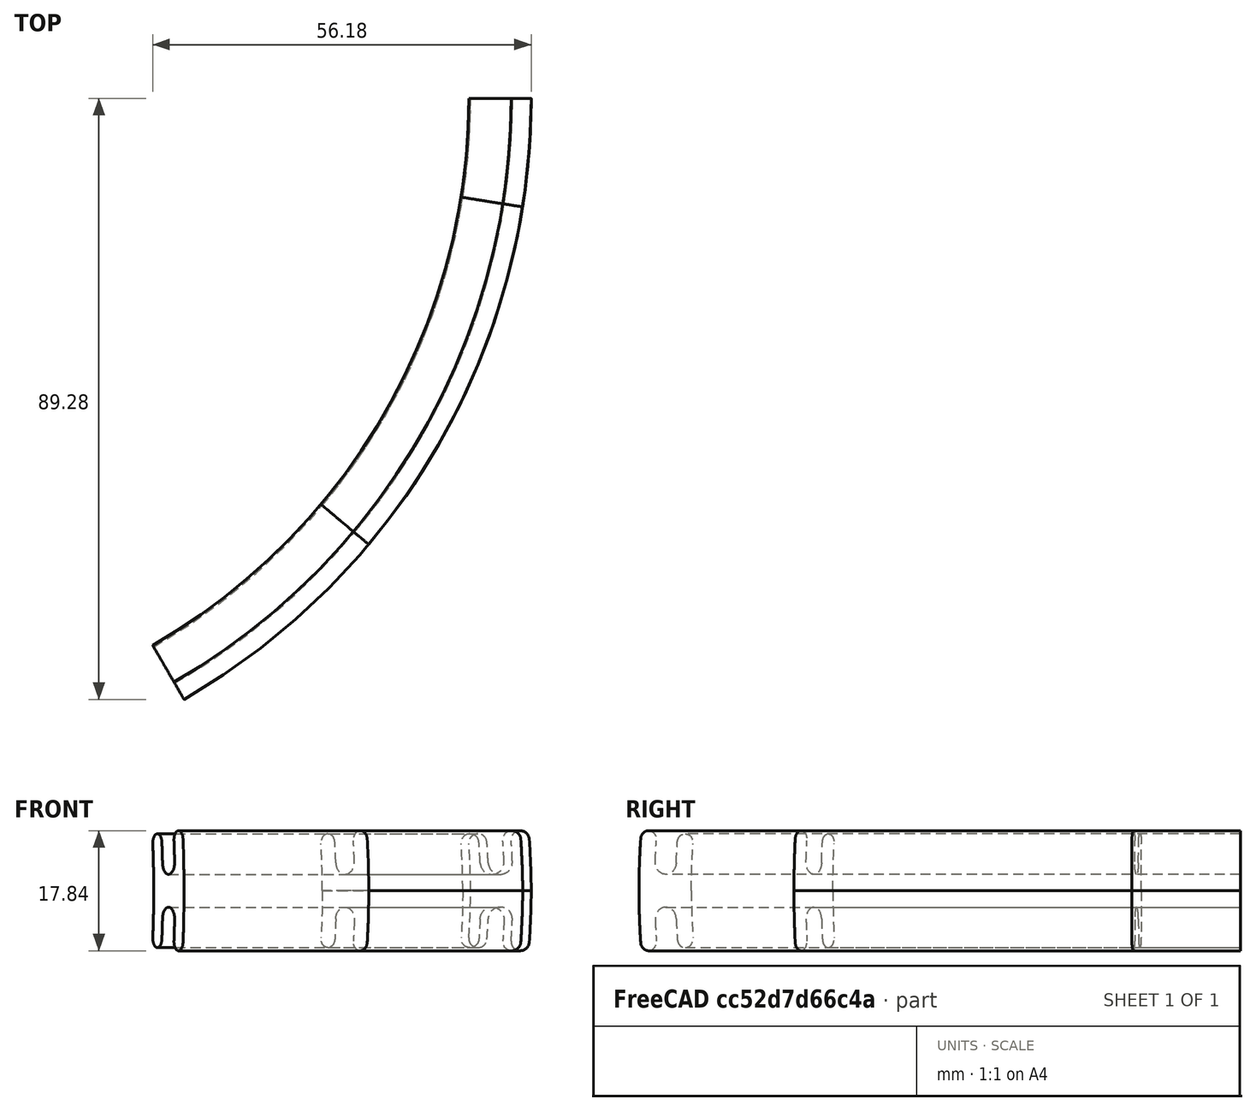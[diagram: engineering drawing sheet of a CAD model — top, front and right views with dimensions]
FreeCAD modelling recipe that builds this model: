
FCSTD DOCUMENT  (FreeCAD 0.16R6707 (Git))
Label: sphere clip
License: All rights reserved
LicenseURL: http://en.wikipedia.org/wiki/All_rights_reserved
objects: Part::Feature×3, Sketcher::SketchObject×2, PartDesign::Revolution×1
note: 7 computed .brp shape members not serialized (recipe doc carries the construction recipe); baked Part::Feature solids carry a one-line shape summary decoded from their .brp

FEATURE [Sketcher::SketchObject] Sketch  label="guide"
  Placement = pos=(0,0,0) rot=(-1,0,0;4.71239rad)
  sketch-geometry (4):
    g0: LineSegment [constr] StartX=0 StartY=4.23777 StartZ=0 EndX=100 EndY=4.23777 EndZ=0
    g1: LineSegment [constr] StartX=0 StartY=96.2378 StartZ=0 EndX=27.5 EndY=96.2378 EndZ=0
    g2: ArcOfCircle [constr] CenterX=0 CenterY=0 CenterZ=0 NormalX=0 NormalY=0 NormalZ=1 Radius=100.09 StartAngle=0 EndAngle=1.5708
    g3: ArcOfCircle [constr] CenterX=0 CenterY=0 CenterZ=0 NormalX=0 NormalY=0 NormalZ=1 Radius=97.0898 StartAngle=0 EndAngle=1.5708
  constraints (17):
    c: PointOnObject(g0,g-2)
    c: Horizontal(g0)
    c: DistanceX(g0,g0) = 100
    c: PointOnObject(g1,g-2)
    c: Horizontal(g1)
    c: DistanceX(g1,g1) = 27.5
    c: DistanceY(g0,g1) = 92
    c: PointOnObject(g2,g-2)
    c: PointOnObject(g2,g-2)
    c: PointOnObject(g2,g-1)
    c: PointOnObject(g1,g2)
    c: PointOnObject(g0,g2)
    c: Coincident(g2,g-1)
    c: Coincident(g3,g-1)
    c: PointOnObject(g3,g-2)
    c: PointOnObject(g3,g-1)
    c: DistanceY(g3,g2) = 3
FEATURE [Sketcher::SketchObject] Sketch001  label="clip profile"
  Placement = pos=(0,0,0) rot=(1,0,0;1.5708rad)
  sketch-geometry (25):
    g0: LineSegment [constr] StartX=0 StartY=4.23777 StartZ=0 EndX=100 EndY=4.23777 EndZ=0
    g1: LineSegment [constr] StartX=0 StartY=96.2378 StartZ=0 EndX=27.5 EndY=96.2378 EndZ=0
    g2: ArcOfCircle [constr] CenterX=0 CenterY=0 CenterZ=0 NormalX=0 NormalY=0 NormalZ=1 Radius=100.09 StartAngle=0 EndAngle=1.5708
    g3: ArcOfCircle [constr] CenterX=0 CenterY=0 CenterZ=0 NormalX=0 NormalY=0 NormalZ=1 Radius=97.0898 StartAngle=0 EndAngle=1.5708
    g4: ArcOfCircle CenterX=98.4986 CenterY=4.23777 CenterZ=0 NormalX=0 NormalY=0 NormalZ=1 Radius=1.8 StartAngle=3.18459 EndAngle=6.32618
    g5: ArcOfCircle CenterX=0 CenterY=0 CenterZ=0 NormalX=0 NormalY=0 NormalZ=1 Radius=96.7898 StartAngle=0.0429971 EndAngle=0.0744659
    g6: ArcOfCircle CenterX=0 CenterY=0 CenterZ=0 NormalX=0 NormalY=0 NormalZ=1 Radius=100.39 StartAngle=0.0429971 EndAngle=0.0744659
    g7: LineSegment [constr] StartX=0 StartY=0 StartZ=0 EndX=96.6082 EndY=5.92521 EndZ=0
    g8: LineSegment [constr] StartX=96.6082 StartY=5.92521 StartZ=0 EndX=100.201 EndY=6.14559 EndZ=0
    g9: LineSegment [constr] StartX=98.3884 StartY=6.0344 StartZ=0 EndX=98.4986 EndY=4.23777 EndZ=0
    g10: LineSegment [constr] StartX=98.4986 StartY=4.23777 StartZ=0 EndX=98.6088 EndY=2.44115 EndZ=0
    g11: LineSegment [constr] StartX=96.8207 StartY=7.22319 StartZ=0 EndX=98.3165 EndY=7.33479 EndZ=0
    g12: LineSegment [constr] StartX=98.3165 StartY=7.33479 StartZ=0 EndX=99.8124 EndY=7.44638 EndZ=0
    g13: LineSegment [constr] StartX=98.2049 StartY=8.83063 StartZ=0 EndX=98.4281 EndY=5.83894 EndZ=0
    g14: LineSegment [constr] StartX=96.5215 StartY=7.20087 StartZ=0 EndX=96.8207 EndY=7.22319 EndZ=0
    g15: LineSegment [constr] StartX=99.8124 StartY=7.44638 StartZ=0 EndX=100.112 EndY=7.4687 EndZ=0
    g16: ArcOfCircle CenterX=0 CenterY=0 CenterZ=0 NormalX=0 NormalY=0 NormalZ=1 Radius=94.0898 StartAngle=0 EndAngle=0.0744659
    g17: ArcOfCircle CenterX=0 CenterY=0 CenterZ=0 NormalX=0 NormalY=0 NormalZ=1 Radius=103.09 StartAngle=0 EndAngle=0.0744659
    g18: LineSegment StartX=94.0898 StartY=0 StartZ=0 EndX=97.0898 EndY=0 EndZ=0
    g19: LineSegment StartX=97.0898 StartY=0 StartZ=0 EndX=100.09 EndY=0 EndZ=0
    g20: LineSegment StartX=100.09 StartY=0 StartZ=0 EndX=103.09 EndY=0 EndZ=0
    g21: LineSegment [constr] StartX=96.5215 StartY=7.20087 StartZ=0 EndX=93.829 EndY=7 EndZ=0
    g22: LineSegment [constr] StartX=100.112 StartY=7.4687 StartZ=0 EndX=102.804 EndY=7.66957 EndZ=0
    g23: ArcOfCircle CenterX=95.1753 CenterY=7.10044 CenterZ=0 NormalX=0 NormalY=0 NormalZ=1 Radius=1.35 StartAngle=0.0744659 EndAngle=3.21606
    g24: ArcOfCircle CenterX=101.458 CenterY=7.56914 CenterZ=0 NormalX=0 NormalY=0 NormalZ=1 Radius=1.35 StartAngle=0.0744659 EndAngle=3.21606
  constraints (79):
    c: PointOnObject(g0,g-2)
    c: Horizontal(g0)
    c: DistanceX(g0,g0) = 100
    c: PointOnObject(g1,g-2)
    c: Horizontal(g1)
    c: DistanceX(g1,g1) = 27.5
    c: DistanceY(g0,g1) = 92
    c: PointOnObject(g2,g-2)
    c: PointOnObject(g2,g-2)
    c: PointOnObject(g2,g-1)
    c: PointOnObject(g1,g2)
    c: PointOnObject(g0,g2)
    c: Coincident(g2,g-1)
    c: Coincident(g3,g-1)
    c: PointOnObject(g3,g-2)
    c: DistanceY(g3,g2) = 3
    c: Coincident(g5,g-1)
    c: Coincident(g5,g4)
    c: Coincident(g6,g-1)
    c: Coincident(g6,g4)
    c: Coincident(g-1,g7)
    c: PointOnObject(g7,g5)
    c: Coincident(g7,g8)
    c: PointOnObject(g8,g6)
    c: Parallel(g7,g8)
    c: PointOnObject(g9,g8)
    c: Coincident(g9,g10)
    c: PointOnObject(g10,g4)
    c: Coincident(g4,g9)
    c: Equal(g9,g10)
    c: Parallel(g10,g9)
    c: Perpendicular(g8,g9)
    c: PointOnObject(g11,g3)
    c: Coincident(g11,g12)
    c: PointOnObject(g12,g2)
    c: Parallel(g11,g12)
    c: Perpendicular(g3,g11)
    c: Equal(g11,g12)
    c: PointOnObject(g11,g13)
    c: Perpendicular(g12,g13)
    c: Symmetric(g5,g6,g13)
    c: Coincident(g14,g5)
    c: Coincident(g14,g11)
    c: Parallel(g14,g11)
    c: Coincident(g15,g12)
    c: Coincident(g15,g6)
    c: Equal(g15,g14)
    c: Distance(g13) = 3
    c: Coincident(g16,g-1)
    c: PointOnObject(g16,g-1)
    c: Coincident(g17,g-1)
    c: PointOnObject(g17,g-1)
    c: Coincident(g18,g16)
    c: Coincident(g18,g3)
    c: Horizontal(g18)
    c: Coincident(g19,g3)
    c: Coincident(g19,g2)
    c: Coincident(g20,g2)
    c: Coincident(g20,g17)
    c: Equal(g18,g20)
    c: DistanceX(g18,g18) = 3
    c: Coincident(g21,g5)
    c: Coincident(g21,g16)
    c: Parallel(g21,g11)
    c: Coincident(g22,g6)
    c: Coincident(g22,g17)
    c: Parallel(g22,g12)
    c: PointOnObject(g23,g21)
    c: Coincident(g5,g23)
    c: PointOnObject(g24,g22)
    c: Coincident(g24,g6)
    c: Coincident(g24,g17)
    c: Coincident(g16,g23)
    c: Tangent(g4,g5)
    c: Tangent(g4,g6)
    c: DistanceY(g16,g16) = 7
    c: Distance(g15) = 0.3
    c: PointOnObject(g4,g0)
    c: Symmetric(g13,g13,g12)
FEATURE [PartDesign::Revolution] Revolution
  Angle = 40
  Axis = (0,0,1)
  Base = (0,0,0)
  Placement = pos=(0,0,0) rot=(1,0,0;1.5708rad)
  ReferenceAxis = -> Sketch001 [V_Axis]
  Reversed = true
  Sketch = -> Sketch001
FEATURE [Part::Feature] Fusion001  label="Fusion9"
  shape: bbox 10.46 x 16.13 x 17.84 mm, 16 faces (baked)
FEATURE [Part::Feature] Fusion002  label="Fusion60"
  shape: bbox 64.37 x 96.37 x 17.84 mm, 16 faces (baked)
FEATURE [Part::Feature] Fusion003  label="Fusion40"
  shape: bbox 39.4 x 71.53 x 17.84 mm, 16 faces (baked)
